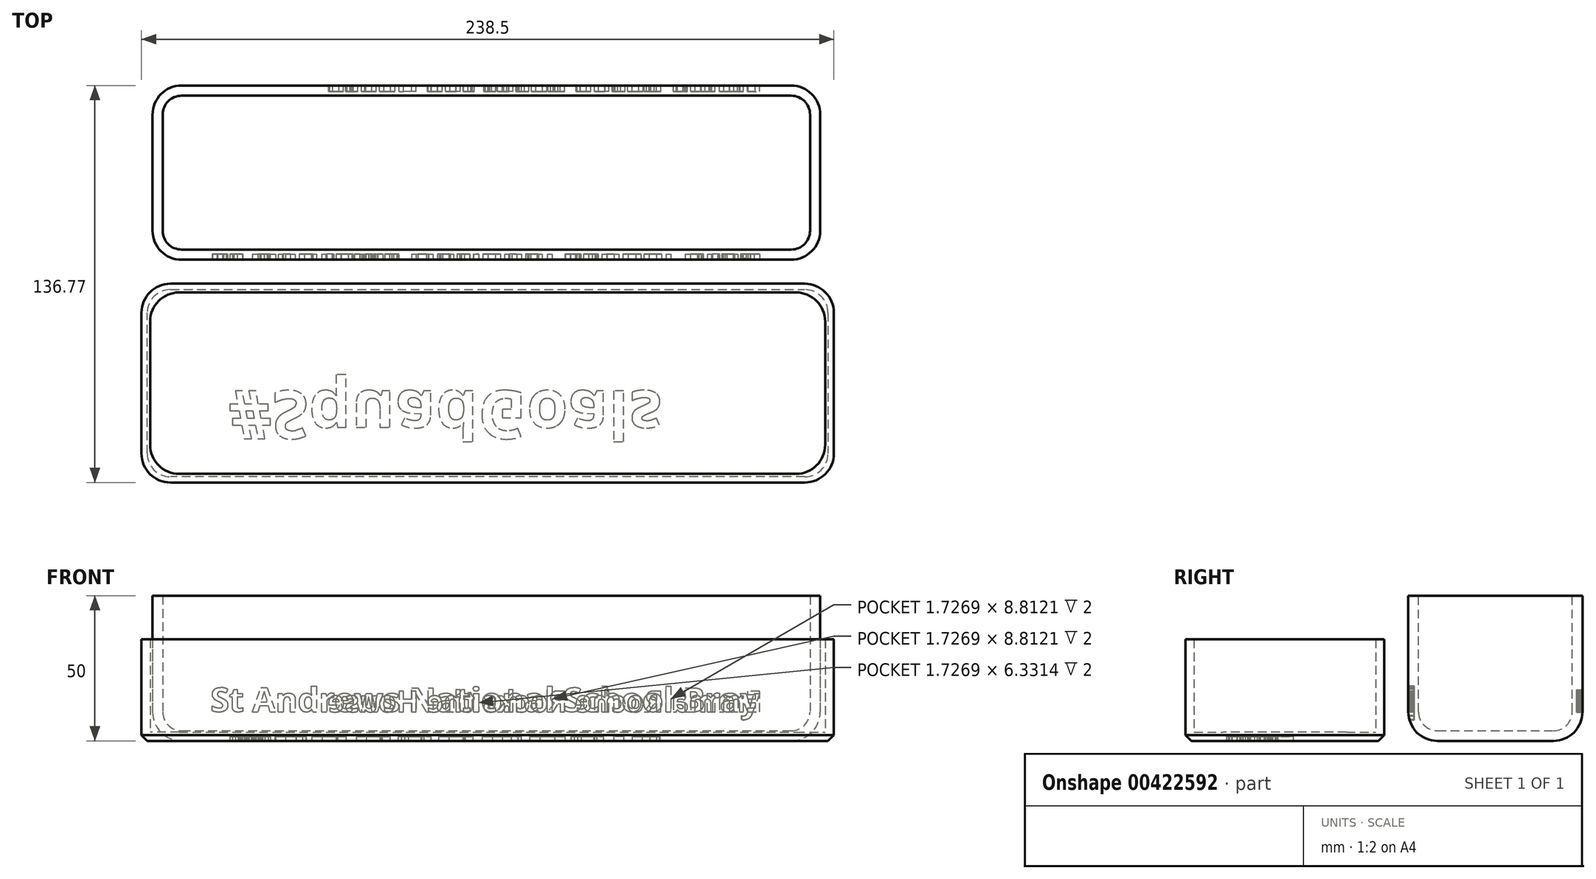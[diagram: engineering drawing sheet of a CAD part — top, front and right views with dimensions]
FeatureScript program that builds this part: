
annotation { "Feature Type Name" : "Feature", "Feature Type Description" : "" }
export const myFeature = defineFeature(function(context is Context, id is Id, definition is map)
    precondition{}
    {
        {
            var Q0;
            Q0=qCreatedBy(makeId("Top.planeOp"),FACE);
            var sketch = newSketch(context, id + "F0", { "sketchPlane" : qUnion([Q0])});
            skLineSegment(sketch, "E0.bottom", {"start": v(-108.23, 18.46) * mm, "end": v(121.77, 18.46) * mm});
            skLineSegment(sketch, "E0.top", {"start": v(-108.23, -41.54) * mm, "end": v(121.77, -41.54) * mm});
            skLineSegment(sketch, "E0.left", {"start": v(-108.23, 18.46) * mm, "end": v(-108.23, -41.54) * mm});
            skLineSegment(sketch, "E0.right", {"start": v(121.77, 18.46) * mm, "end": v(121.77, -41.54) * mm});
            skSolve(sketch);
        }
        {
            var Q0;
            Q0=makeQuery(id+"F0.imprint","IMPRINT",FACE,{"disambiguationData":[TD([[makeQuery(id+"F0.imprint","IMPRINT",EDGE,{"derivedFrom":sQuery(id+"F0.wireOp",EDGE,"E0.bottom")}),-1.0]])]});
            extrude(context, id + "F1", {"entities" : qUnion([Q0]), "depth" : 50 * mm});
        }
        {
            var Q0;
            Q0=makeQuery(id+"F1.opExtrude","SWEPT_EDGE",EDGE,{"disambiguationData":[OSD([sQuery(id+"F0.wireOp",EDGE,"E0.top"),sQuery(id+"F0.wireOp",EDGE,"E0.left")])]});
            fillet(context, id + "F2", {"entities" : qUnion([Q0]), "radius" : 10 * mm, "tangentPropagation" : true, "allowEdgeOverflow" : false});
        }
        {
            var Q0;
            Q0=makeQuery(id+"F1.opExtrude","SWEPT_EDGE",EDGE,{"disambiguationData":[OSD([sQuery(id+"F0.wireOp",EDGE,"E0.top"),sQuery(id+"F0.wireOp",EDGE,"E0.right")])]});
            var Q1;
            Q1=makeQuery(id+"F1.opExtrude","SWEPT_EDGE",EDGE,{"disambiguationData":[OSD([sQuery(id+"F0.wireOp",EDGE,"E0.bottom"),sQuery(id+"F0.wireOp",EDGE,"E0.right")])]});
            var Q2;
            Q2=makeQuery(id+"F1.opExtrude","SWEPT_EDGE",EDGE,{"disambiguationData":[OSD([sQuery(id+"F0.wireOp",EDGE,"E0.bottom"),sQuery(id+"F0.wireOp",EDGE,"E0.left")])]});
            var Q3;
            Q3=makeQuery(id+"F1.opExtrude","CAP_EDGE",EDGE,{"disambiguationData":[OSD([sQuery(id+"F0.wireOp",EDGE,"E0.top")])],"isStart":true});
            var Q4;
            Q4=makeQuery(id+"F1.opExtrude","CAP_EDGE",EDGE,{"disambiguationData":[OSD([sQuery(id+"F0.wireOp",EDGE,"E0.bottom")])],"isStart":true});
            var Q5;
            Q5=makeQuery(id+"F1.opExtrude","CAP_EDGE",EDGE,{"disambiguationData":[OSD([sQuery(id+"F0.wireOp",EDGE,"E0.right")])],"isStart":true});
            fillet(context, id + "F3", {"entities" : qUnion([Q0, Q1, Q2, Q3, Q4, Q5]), "radius" : 10 * mm, "tangentPropagation" : true, "allowEdgeOverflow" : false});
        }
        {
            var Q0;
            Q0=makeQuery(id+"F1.opExtrude","CAP_FACE",FACE,{"disambiguationData":[OSD([sQuery(id+"F0.wireOp",EDGE,"E0.bottom"),sQuery(id+"F0.wireOp",EDGE,"E0.top"),sQuery(id+"F0.wireOp",EDGE,"E0.left"),sQuery(id+"F0.wireOp",EDGE,"E0.right")])],"isStart":false});
            shell(context, id + "F4", {"entities" : qUnion([Q0]), "thickness" : 3.5 * mm});
        }
        {
            var Q0;
            Q0=makeQuery(id+"F1.opExtrude","SWEPT_FACE",FACE,{"disambiguationData":[OSD([sQuery(id+"F0.wireOp",EDGE,"E0.bottom")])]});
            var sketch = newSketch(context, id + "F5", { "sketchPlane" : qUnion([Q0])});
            skText(sketch, "E1", { "text": "Emma Roche Rocks the House", "fontName": "OpenSans-Bold.ttf"});
            const initialGuessF5  = {"E1": [-0.10177, 0.01, 1, 0, 0.00722]};
            skSetInitialGuess(sketch, initialGuessF5);
            skSolve(sketch);
        }
        {
            var Q0;
            Q0=makeQuery(id+"F1.opExtrude","SWEPT_FACE",FACE,{"disambiguationData":[OSD([sQuery(id+"F0.wireOp",EDGE,"E0.top")])]});
            var sketch = newSketch(context, id + "F6", { "sketchPlane" : qUnion([Q0])});
            skText(sketch, "E2", { "text": "St Andrews National School Bray", "fontName": "OpenSans-Bold.ttf"});
            const initialGuessF6  = {"E2": [-0.08823, 0.01, 1, 0, 0.00835]};
            skSetInitialGuess(sketch, initialGuessF6);
            skSolve(sketch);
        }
        {
            var Q0;
            Q0 = qSketchRegion(id + "F5", true);
            extrude(context, id + "F7", {"entities" : qUnion([Q0]), "operationType" : NewBodyOperationType.REMOVE, "oppositeDirection" : true, "depth" : 2 * mm});
        }
        {
            var Q0;
            Q0 = qSketchRegion(id + "F6", true);
            extrude(context, id + "F8", {"entities" : qUnion([Q0]), "operationType" : NewBodyOperationType.REMOVE, "oppositeDirection" : true, "depth" : 2 * mm});
        }
        {
            var Q0;
            Q0=qCreatedBy(makeId("Top.planeOp"),FACE);
            var sketch = newSketch(context, id + "F9", { "sketchPlane" : qUnion([Q0])});
            skLineSegment(sketch, "E3.bottom", {"start": v(-104.54, -39.81) * mm, "end": v(133.96, -39.81) * mm});
            skLineSegment(sketch, "E3.top", {"start": v(-104.54, -108.31) * mm, "end": v(133.96, -108.31) * mm});
            skLineSegment(sketch, "E3.left", {"start": v(-104.54, -39.81) * mm, "end": v(-104.54, -108.31) * mm});
            skLineSegment(sketch, "E3.right", {"start": v(133.96, -39.81) * mm, "end": v(133.96, -108.31) * mm});
            skSolve(sketch);
        }
        {
            var Q0;
            Q0=makeQuery(id+"F9.imprint","IMPRINT",FACE,{"disambiguationData":[TD([[makeQuery(id+"F9.imprint","IMPRINT",EDGE,{"derivedFrom":sQuery(id+"F9.wireOp",EDGE,"E3.bottom")}),-1.0]])]});
            extrude(context, id + "F10", {"entities" : qUnion([Q0]), "depth" : 35 * mm});
        }
        {
            var Q0;
            Q0=makeQuery(id+"F10.opExtrude","CAP_FACE",FACE,{"disambiguationData":[OSD([sQuery(id+"F9.wireOp",EDGE,"E3.bottom"),sQuery(id+"F9.wireOp",EDGE,"E3.top"),sQuery(id+"F9.wireOp",EDGE,"E3.left"),sQuery(id+"F9.wireOp",EDGE,"E3.right")])],"isStart":false});
            shell(context, id + "F11", {"entities" : qUnion([Q0]), "thickness" : 3 * mm});
        }
        {
            var Q0;
            Q0=makeQuery(id+"F11.opShell","OFFSET_EDGE",EDGE,{"disambiguationData":[OSD([sQuery(id+"F9.wireOp",EDGE,"E3.bottom"),sQuery(id+"F9.wireOp",EDGE,"E3.left")])]});
            var Q1;
            Q1=makeQuery(id+"F11.opShell","OFFSET_EDGE",EDGE,{"disambiguationData":[OSD([sQuery(id+"F9.wireOp",EDGE,"E3.top"),sQuery(id+"F9.wireOp",EDGE,"E3.left")])]});
            var Q2;
            Q2=makeQuery(id+"F11.opShell","OFFSET_EDGE",EDGE,{"disambiguationData":[OSD([sQuery(id+"F9.wireOp",EDGE,"E3.bottom"),sQuery(id+"F9.wireOp",EDGE,"E3.right")])]});
            var Q3;
            Q3=makeQuery(id+"F11.opShell","OFFSET_EDGE",EDGE,{"disambiguationData":[OSD([sQuery(id+"F9.wireOp",EDGE,"E3.top"),sQuery(id+"F9.wireOp",EDGE,"E3.right")])]});
            var Q4;
            Q4=makeQuery(id+"F10.opExtrude","SWEPT_EDGE",EDGE,{"disambiguationData":[OSD([sQuery(id+"F9.wireOp",EDGE,"E3.bottom"),sQuery(id+"F9.wireOp",EDGE,"E3.left")])]});
            var Q5;
            Q5=makeQuery(id+"F10.opExtrude","SWEPT_EDGE",EDGE,{"disambiguationData":[OSD([sQuery(id+"F9.wireOp",EDGE,"E3.top"),sQuery(id+"F9.wireOp",EDGE,"E3.left")])]});
            var Q6;
            Q6=makeQuery(id+"F10.opExtrude","SWEPT_EDGE",EDGE,{"disambiguationData":[OSD([sQuery(id+"F9.wireOp",EDGE,"E3.top"),sQuery(id+"F9.wireOp",EDGE,"E3.right")])]});
            var Q7;
            Q7=makeQuery(id+"F10.opExtrude","SWEPT_EDGE",EDGE,{"disambiguationData":[OSD([sQuery(id+"F9.wireOp",EDGE,"E3.bottom"),sQuery(id+"F9.wireOp",EDGE,"E3.right")])]});
            fillet(context, id + "F12", {"entities" : qUnion([Q0, Q1, Q2, Q3, Q4, Q5, Q6, Q7]), "radius" : 10 * mm, "tangentPropagation" : true, "allowEdgeOverflow" : false});
        }
        {
            var Q0;
            Q0=makeQuery(id+"F10.opExtrude","CAP_FACE",FACE,{"disambiguationData":[OSD([sQuery(id+"F9.wireOp",EDGE,"E3.bottom"),sQuery(id+"F9.wireOp",EDGE,"E3.top"),sQuery(id+"F9.wireOp",EDGE,"E3.left"),sQuery(id+"F9.wireOp",EDGE,"E3.right")])],"isStart":true});
            var sketch = newSketch(context, id + "F13", { "sketchPlane" : qUnion([Q0])});
            skText(sketch, "E4", { "text": "#SquadGoals", "fontName": "OpenSans-Bold.ttf"});
            const initialGuessF13  = {"E4": [-0.07454, 0.0767, 1, 0, 0.01662]};
            skSetInitialGuess(sketch, initialGuessF13);
            skSolve(sketch);
        }
        {
            var Q0;
            Q0 = qSketchRegion(id + "F13", true);
            extrude(context, id + "F14", {"entities" : qUnion([Q0]), "operationType" : NewBodyOperationType.REMOVE, "oppositeDirection" : true, "depth" : 1.5 * mm});
        }
        {
            var Q0;
            Q0=makeQuery(id+"F10.opExtrude","CAP_EDGE",EDGE,{"disambiguationData":[OSD([sQuery(id+"F9.wireOp",EDGE,"E3.top")])],"isStart":true});
            chamfer(context, id + "F15", {"entities" : qUnion([Q0]), "width" : 2 * mm, "tangentPropagation" : true});
        }
        {
            var Q0;
            Q0=makeQuery(id+"F10.opExtrude","SWEPT_BODY",BODY,{"disambiguationData":[OSD([sQuery(id+"F9.wireOp",EDGE,"E3.bottom"),sQuery(id+"F9.wireOp",EDGE,"E3.top"),sQuery(id+"F9.wireOp",EDGE,"E3.left"),sQuery(id+"F9.wireOp",EDGE,"E3.right")])]});
            transform(context, id + "F16", {"entities" : qUnion([Q0]), "transformType" : TransformType.TRANSLATION_3D, "dx" : -7.5 * mm, "dy" : -10 * mm, "dz" : 0 * mm, "makeCopy" : false});
        }
    });
